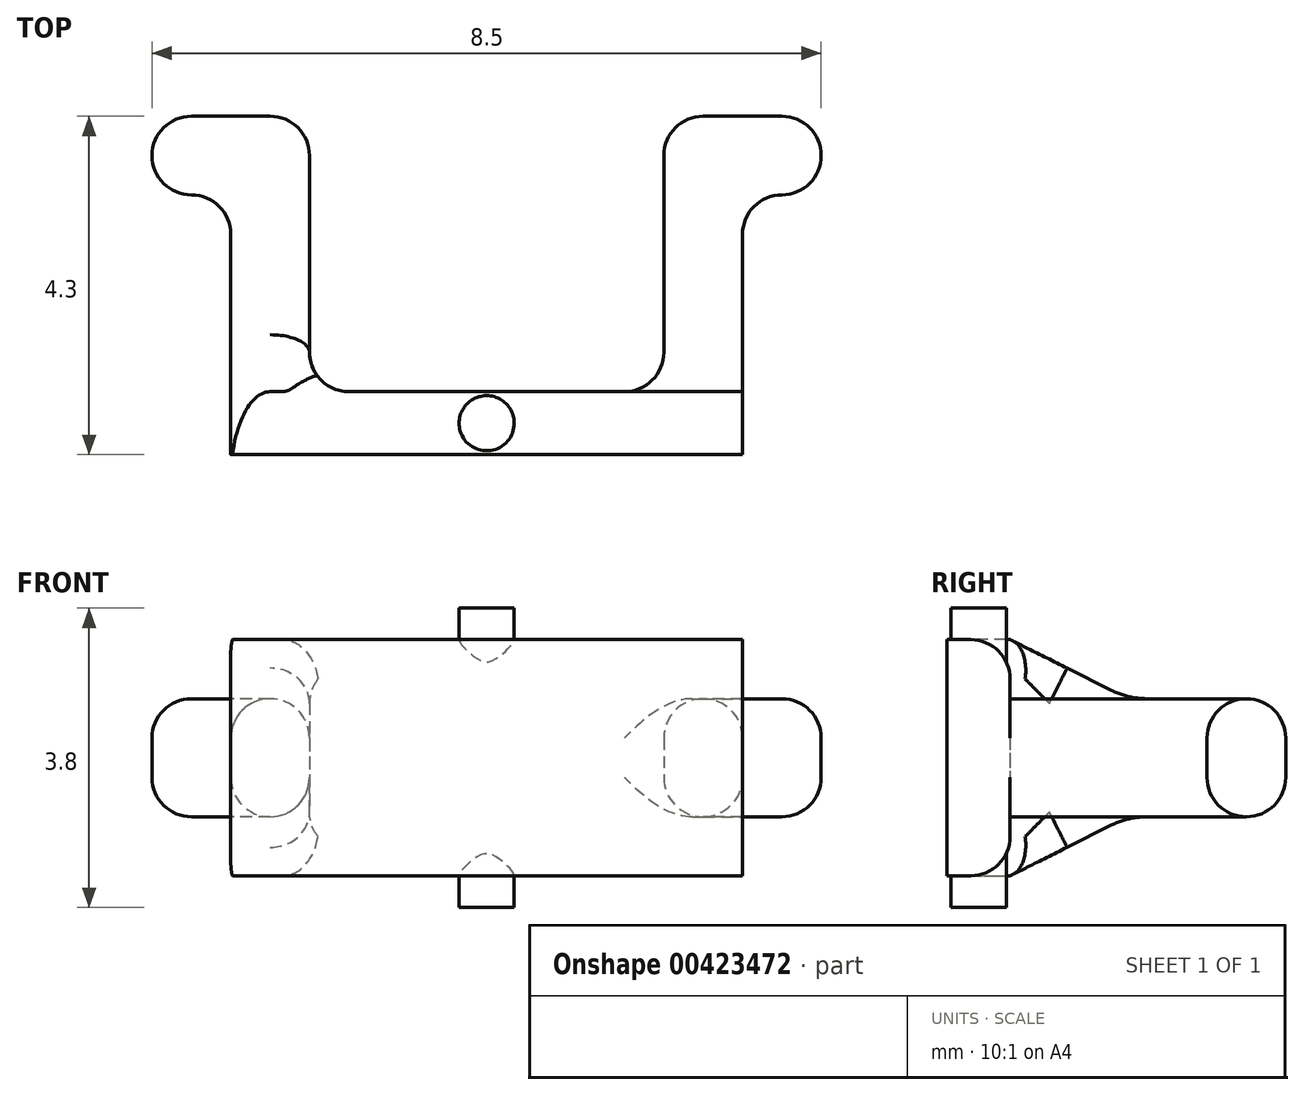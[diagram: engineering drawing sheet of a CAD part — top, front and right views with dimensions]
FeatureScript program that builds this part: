
annotation { "Feature Type Name" : "Feature", "Feature Type Description" : "" }
export const myFeature = defineFeature(function(context is Context, id is Id, definition is map)
    precondition{}
    {
        {
            var Q0;
            Q0=qCreatedBy(makeId("Top.planeOp"),FACE);
            var sketch = newSketch(context, id + "F0", { "sketchPlane" : qUnion([Q0])});
            skLineSegment(sketch, "E0", {"start": v(-3.25, 0) * mm, "end": v(3.25, 0) * mm});
            skPoint(sketch, "E1", {"position": v(0, 0) * mm});
            skLineSegment(sketch, "E2", {"start": v(0, -3) * mm, "end": v(0, 7.11) * mm, "construction": true});
            skLineSegment(sketch, "E3", {"start": v(2.25, 1.3) * mm, "end": v(2.25, 3.8) * mm});
            skLineSegment(sketch, "E4", {"start": v(-2.25, 1.3) * mm, "end": v(-2.25, 3.8) * mm});
            skLineSegment(sketch, "E5", {"start": v(-1.75, 0.8) * mm, "end": v(1.75, 0.8) * mm});
            skPoint(sketch, "E6", {"position": v(0, 0.8) * mm});
            skLineSegment(sketch, "E7", {"start": v(-2.75, 4.3) * mm, "end": v(-3.75, 4.3) * mm});
            skLineSegment(sketch, "E8", {"start": v(2.75, 4.3) * mm, "end": v(3.75, 4.3) * mm});
            skLineSegment(sketch, "E9", {"start": v(-4.25, 3.8) * mm, "end": v(-4.25, 3.8) * mm});
            skLineSegment(sketch, "E10", {"start": v(-3.75, 3.3) * mm, "end": v(-3.75, 3.3) * mm});
            skLineSegment(sketch, "E11", {"start": v(-3.25, 2.8) * mm, "end": v(-3.25, 0) * mm});
            skLineSegment(sketch, "E12", {"start": v(4.25, 3.8) * mm, "end": v(4.25, 3.8) * mm});
            skLineSegment(sketch, "E13", {"start": v(3.75, 3.3) * mm, "end": v(3.75, 3.3) * mm});
            skLineSegment(sketch, "E14", {"start": v(3.25, 2.8) * mm, "end": v(3.25, 0) * mm});
            skPoint(sketch, "E15.visualSharp", {"position": v(-2.25, 0.8) * mm});
            skArc(sketch, "E15.filletArc", {"start": v(-2.25, 1.3) * mm, "mid": v(-2.1, 0.95) * mm, "end": v(-1.75, 0.8) * mm});
            skPoint(sketch, "E16.visualSharp", {"position": v(2.25, 0.8) * mm});
            skArc(sketch, "E16.filletArc", {"start": v(1.75, 0.8) * mm, "mid": v(2.1, 0.95) * mm, "end": v(2.25, 1.3) * mm});
            skPoint(sketch, "E17.visualSharp", {"position": v(3.25, 3.3) * mm});
            skArc(sketch, "E17.filletArc", {"start": v(3.75, 3.3) * mm, "mid": v(3.4, 3.15) * mm, "end": v(3.25, 2.8) * mm});
            skPoint(sketch, "E18.visualSharp", {"position": v(-3.25, 3.3) * mm});
            skArc(sketch, "E18.filletArc", {"start": v(-3.25, 2.8) * mm, "mid": v(-3.4, 3.15) * mm, "end": v(-3.75, 3.3) * mm});
            skPoint(sketch, "E19.visualSharp", {"position": v(-2.25, 4.3) * mm});
            skArc(sketch, "E19.filletArc", {"start": v(-2.25, 3.8) * mm, "mid": v(-2.4, 4.15) * mm, "end": v(-2.75, 4.3) * mm});
            skPoint(sketch, "E20.visualSharp", {"position": v(2.25, 4.3) * mm});
            skArc(sketch, "E20.filletArc", {"start": v(2.75, 4.3) * mm, "mid": v(2.4, 4.15) * mm, "end": v(2.25, 3.8) * mm});
            skPoint(sketch, "E21.visualSharp", {"position": v(4.25, 4.3) * mm});
            skArc(sketch, "E21.filletArc", {"start": v(4.25, 3.8) * mm, "mid": v(4.1, 4.15) * mm, "end": v(3.75, 4.3) * mm});
            skPoint(sketch, "E22.visualSharp", {"position": v(4.25, 3.3) * mm});
            skArc(sketch, "E22.filletArc", {"start": v(3.75, 3.3) * mm, "mid": v(4.1, 3.45) * mm, "end": v(4.25, 3.8) * mm});
            skPoint(sketch, "E23.visualSharp", {"position": v(-4.25, 4.3) * mm});
            skArc(sketch, "E23.filletArc", {"start": v(-3.75, 4.3) * mm, "mid": v(-4.1, 4.15) * mm, "end": v(-4.25, 3.8) * mm});
            skPoint(sketch, "E24.visualSharp", {"position": v(-4.25, 3.3) * mm});
            skArc(sketch, "E24.filletArc", {"start": v(-4.25, 3.8) * mm, "mid": v(-4.1, 3.45) * mm, "end": v(-3.75, 3.3) * mm});
            skPoint(sketch, "E25.orphan", {"position": v(5, 0) * mm});
            skSolve(sketch);
        }
        {
            var Q0;
            Q0=qSketchRegion(id+"F0",true);
            extrude(context, id + "F1", {"entities" : qUnion([Q0]), "depth" : 1.5 * mm, "offsetDistance" : 25 * mm});
        }
        {
            var Q0;
            Q0=makeQuery(id+"F1.opExtrude","CAP_FACE",FACE,{"disambiguationData":[OSD([sQuery(id+"F0.wireOp",EDGE,"E0"),sQuery(id+"F0.wireOp",EDGE,"6YUp3G7D-HScl-yHn5-GseC-h8JY3a3RTnfq"),sQuery(id+"F0.wireOp",EDGE,"Xoj59s7T-2QtX-ZDX5-LiLJ-oQHR1xyVejqm"),sQuery(id+"F0.wireOp",EDGE,"Zc0sCTJD-TUej-OjTx-Aevo-d0EqPVeEhSTX"),sQuery(id+"F0.wireOp",EDGE,"E3"),sQuery(id+"F0.wireOp",EDGE,"E4"),sQuery(id+"F0.wireOp",EDGE,"fb0ed693-0343-43f7-9de8-dc647e30bef6.trimOffspring"),sQuery(id+"F0.wireOp",EDGE,"E5"),sQuery(id+"F0.wireOp",EDGE,"E7"),sQuery(id+"F0.wireOp",EDGE,"E8"),sQuery(id+"F0.wireOp",EDGE,"E15.filletArc"),sQuery(id+"F0.wireOp",EDGE,"E16.filletArc"),sQuery(id+"F0.wireOp",EDGE,"e3a1806a-2c86-475e-80ef-7f3d2f1d7afe.filletArc"),sQuery(id+"F0.wireOp",EDGE,"E17.filletArc"),sQuery(id+"F0.wireOp",EDGE,"63802826-9469-4e69-9e87-4bd683e02e6c.filletArc"),sQuery(id+"F0.wireOp",EDGE,"E18.filletArc"),sQuery(id+"F0.wireOp",EDGE,"E19.filletArc"),sQuery(id+"F0.wireOp",EDGE,"E20.filletArc"),sQuery(id+"F0.wireOp",EDGE,"E21.filletArc"),sQuery(id+"F0.wireOp",EDGE,"E22.filletArc"),sQuery(id+"F0.wireOp",EDGE,"E23.filletArc"),sQuery(id+"F0.wireOp",EDGE,"E24.filletArc")])],"isStart":false});
            var sketch = newSketch(context, id + "F2", { "sketchPlane" : qUnion([Q0])});
            skLineSegment(sketch, "E26.0", {"start": v(-3.25, 0) * mm, "end": v(-3.25, 0) * mm});
            skLineSegment(sketch, "E27.0", {"start": v(-3.25, 0) * mm, "end": v(-3.25, 0.8) * mm});
            skLineSegment(sketch, "E28", {"start": v(-3.25, 0.8) * mm, "end": v(3.25, 0.8) * mm});
            skLineSegment(sketch, "E29.0", {"start": v(-3.25, 0) * mm, "end": v(3.25, 0) * mm});
            skLineSegment(sketch, "E30.0", {"start": v(3.25, 0.8) * mm, "end": v(3.25, 0) * mm});
            skPoint(sketch, "E31.orphan", {"position": v(3.25, 2.8) * mm});
            skSolve(sketch);
        }
        {
            var Q0;
            Q0=qSketchRegion(id+"F2",true);
            extrude(context, id + "F3", {"entities" : qUnion([Q0]), "operationType" : NewBodyOperationType.ADD, "depth" : 0.75 * mm, "offsetDistance" : 25 * mm});
        }
        {
            var Q0;
            Q0=makeQuery(id+"F1.opExtrude","CAP_FACE",FACE,{"disambiguationData":[OSD([sQuery(id+"F0.wireOp",EDGE,"E0"),sQuery(id+"F0.wireOp",EDGE,"E3"),sQuery(id+"F0.wireOp",EDGE,"E4"),sQuery(id+"F0.wireOp",EDGE,"E5"),sQuery(id+"F0.wireOp",EDGE,"E7"),sQuery(id+"F0.wireOp",EDGE,"E8"),sQuery(id+"F0.wireOp",EDGE,"E11"),sQuery(id+"F0.wireOp",EDGE,"E14"),sQuery(id+"F0.wireOp",EDGE,"E15.filletArc"),sQuery(id+"F0.wireOp",EDGE,"E16.filletArc"),sQuery(id+"F0.wireOp",EDGE,"E17.filletArc"),sQuery(id+"F0.wireOp",EDGE,"E18.filletArc"),sQuery(id+"F0.wireOp",EDGE,"E19.filletArc"),sQuery(id+"F0.wireOp",EDGE,"E20.filletArc"),sQuery(id+"F0.wireOp",EDGE,"E21.filletArc"),sQuery(id+"F0.wireOp",EDGE,"E22.filletArc"),sQuery(id+"F0.wireOp",EDGE,"E23.filletArc"),sQuery(id+"F0.wireOp",EDGE,"E24.filletArc")])],"isStart":true});
            var sketch = newSketch(context, id + "F4", { "sketchPlane" : qUnion([Q0])});
            skLineSegment(sketch, "E32.0", {"start": v(-3.25, 0) * mm, "end": v(-3.25, -0.8) * mm});
            skLineSegment(sketch, "E33.0", {"start": v(-3.25, -0.8) * mm, "end": v(3.25, -0.8) * mm});
            skLineSegment(sketch, "E34.0", {"start": v(-3.25, 0) * mm, "end": v(3.25, 0) * mm});
            skLineSegment(sketch, "E35.0", {"start": v(3.25, -0.8) * mm, "end": v(3.25, 0) * mm});
            skSolve(sketch);
        }
        {
            var Q0;
            Q0=qSketchRegion(id+"F4",true);
            extrude(context, id + "F5", {"entities" : qUnion([Q0]), "operationType" : NewBodyOperationType.ADD, "depth" : 0.75 * mm, "offsetDistance" : 25 * mm});
        }
        {
            var Q0;
            {var subQ4=sQuery(id+"F0.wireOp",EDGE,"E15.filletArc");var subQ5=sQuery(id+"F2.wireOp",EDGE,"E28");Q0=makeQuery(id+"F3.boolean.opBoolean","SPLIT",EDGE,{"disambiguationData":[TD([makeQuery(id+"F1.opExtrude","SWEPT_FACE",FACE,{"disambiguationData":[OSD([subQ4])]})])],"derivedFrom":makeQuery(id+"F3.opExtrude","CAP_EDGE",EDGE,{"disambiguationData":[OSD([subQ5])],"isStart":true})});}
            var Q1;
            {var subQ3=sQuery(id+"F0.wireOp",EDGE,"E16.filletArc");var subQ5=sQuery(id+"F2.wireOp",EDGE,"E28");Q1=makeQuery(id+"F3.boolean.opBoolean","SPLIT",EDGE,{"disambiguationData":[TD([makeQuery(id+"F1.opExtrude","SWEPT_FACE",FACE,{"disambiguationData":[OSD([subQ3])]})])],"derivedFrom":makeQuery(id+"F3.opExtrude","CAP_EDGE",EDGE,{"disambiguationData":[OSD([subQ5])],"isStart":true})});}
            chamfer(context, id + "F6", {"entities" : qUnion([Q0, Q1]), "chamferType" : ChamferType.TWO_OFFSETS, "width1" : 1.5 * mm, "oppositeDirection" : false, "width2" : 0.75 * mm, "tangentPropagation" : true});
        }
        {
            var Q0;
            {var subQ0=sQuery(id+"F0.wireOp",EDGE,"E14");var subQ1=sQuery(id+"F4.wireOp",EDGE,"E33.0");Q0=makeQuery(id+"F5.boolean.opBoolean","SPLIT",EDGE,{"disambiguationData":[TD([makeQuery(id+"F1.opExtrude","SWEPT_FACE",FACE,{"disambiguationData":[OSD([subQ0])]})])],"derivedFrom":makeQuery(id+"F5.opExtrude","CAP_EDGE",EDGE,{"disambiguationData":[OSD([subQ1])],"isStart":true})});}
            var Q1;
            {var subQ0=sQuery(id+"F0.wireOp",EDGE,"E11");var subQ3=sQuery(id+"F4.wireOp",EDGE,"E33.0");Q1=makeQuery(id+"F5.boolean.opBoolean","SPLIT",EDGE,{"disambiguationData":[TD([makeQuery(id+"F1.opExtrude","SWEPT_FACE",FACE,{"disambiguationData":[OSD([subQ0])]})])],"derivedFrom":makeQuery(id+"F5.opExtrude","CAP_EDGE",EDGE,{"disambiguationData":[OSD([subQ3])],"isStart":true})});}
            chamfer(context, id + "F7", {"entities" : qUnion([Q0, Q1]), "chamferType" : ChamferType.TWO_OFFSETS, "width1" : 1.5 * mm, "oppositeDirection" : true, "width2" : 0.75 * mm, "tangentPropagation" : true});
        }
        {
            var Q0;
            {var subQ0=sQuery(id+"F0.wireOp",EDGE,"E20.filletArc");var subQ1=sQuery(id+"F0.wireOp",EDGE,"e3a1806a-2c86-475e-80ef-7f3d2f1d7afe.filletArc");var subQ3=sQuery(id+"F0.wireOp",EDGE,"E14");var subQ4=sQuery(id+"F0.wireOp",EDGE,"E8");var subQ5=sQuery(id+"F0.wireOp",EDGE,"E16.filletArc");var subQ6=makeQuery(id+"F1.opExtrude","SWEPT_FACE",FACE,{"disambiguationData":[OSD([subQ5])]});var subQ7=sQuery(id+"F0.wireOp",EDGE,"Xoj59s7T-2QtX-ZDX5-LiLJ-oQHR1xyVejqm");var subQ9=sQuery(id+"F0.wireOp",EDGE,"E5");var subQ11=sQuery(id+"F2.wireOp",EDGE,"E28");var subQ13=sQuery(id+"F0.wireOp",EDGE,"E17.filletArc");var subQ14=sQuery(id+"F0.wireOp",EDGE,"E3");var subQ15=sQuery(id+"F0.wireOp",EDGE,"fb0ed693-0343-43f7-9de8-dc647e30bef6.trimOffspring");var subQ17=sQuery(id+"F0.wireOp",EDGE,"E22.filletArc");var subQ18=sQuery(id+"F0.wireOp",EDGE,"E21.filletArc");var subQ19=makeQuery(id+"F1.opExtrude","CAP_FACE",FACE,{"disambiguationData":[OSD([sQuery(id+"F0.wireOp",EDGE,"E0"),sQuery(id+"F0.wireOp",EDGE,"6YUp3G7D-HScl-yHn5-GseC-h8JY3a3RTnfq"),subQ7,sQuery(id+"F0.wireOp",EDGE,"Zc0sCTJD-TUej-OjTx-Aevo-d0EqPVeEhSTX"),subQ14,sQuery(id+"F0.wireOp",EDGE,"E4"),subQ15,subQ9,sQuery(id+"F0.wireOp",EDGE,"E7"),subQ4,sQuery(id+"F0.wireOp",EDGE,"E11"),subQ3,sQuery(id+"F0.wireOp",EDGE,"E15.filletArc"),subQ5,subQ1,subQ13,sQuery(id+"F0.wireOp",EDGE,"63802826-9469-4e69-9e87-4bd683e02e6c.filletArc"),sQuery(id+"F0.wireOp",EDGE,"E18.filletArc"),sQuery(id+"F0.wireOp",EDGE,"E19.filletArc"),subQ0,subQ18,subQ17,sQuery(id+"F0.wireOp",EDGE,"E23.filletArc"),sQuery(id+"F0.wireOp",EDGE,"E24.filletArc")])],"isStart":false});Q0=makeQuery(id+"F6.opChamfer","BLEND_EDGE",EDGE,{"blendedFrom":[makeQuery(id+"F3.boolean.opBoolean","SPLIT",EDGE,{"disambiguationData":[TD([subQ6])],"derivedFrom":makeQuery(id+"F3.opExtrude","CAP_EDGE",EDGE,{"disambiguationData":[OSD([subQ11])],"isStart":true})}),makeQuery(id+"F3.boolean.opBoolean","SPLIT",FACE,{"disambiguationData":[TD([makeQuery(id+"F1.opExtrude","SWEPT_FACE",FACE,{"disambiguationData":[OSD([subQ14])]})])],"derivedFrom":subQ19})],"blendedInto":[makeQuery(id+"F3.boolean.opBoolean","SPLIT",FACE,{"disambiguationData":[TD([makeQuery(id+"F1.opExtrude","SWEPT_FACE",FACE,{"disambiguationData":[OSD([subQ14])]})])],"derivedFrom":subQ19})]});}
            var Q1;
            {var subQ0=sQuery(id+"F0.wireOp",EDGE,"E15.filletArc");var subQ1=makeQuery(id+"F1.opExtrude","SWEPT_FACE",FACE,{"disambiguationData":[OSD([subQ0])]});var subQ2=sQuery(id+"F0.wireOp",EDGE,"E11");var subQ3=sQuery(id+"F0.wireOp",EDGE,"E7");var subQ4=sQuery(id+"F0.wireOp",EDGE,"Xoj59s7T-2QtX-ZDX5-LiLJ-oQHR1xyVejqm");var subQ6=sQuery(id+"F0.wireOp",EDGE,"E19.filletArc");var subQ7=sQuery(id+"F0.wireOp",EDGE,"E5");var subQ9=sQuery(id+"F2.wireOp",EDGE,"E28");var subQ11=sQuery(id+"F0.wireOp",EDGE,"63802826-9469-4e69-9e87-4bd683e02e6c.filletArc");var subQ13=sQuery(id+"F0.wireOp",EDGE,"E4");var subQ14=sQuery(id+"F0.wireOp",EDGE,"E18.filletArc");var subQ15=sQuery(id+"F0.wireOp",EDGE,"fb0ed693-0343-43f7-9de8-dc647e30bef6.trimOffspring");var subQ17=sQuery(id+"F0.wireOp",EDGE,"E24.filletArc");var subQ18=sQuery(id+"F0.wireOp",EDGE,"E23.filletArc");var subQ19=makeQuery(id+"F1.opExtrude","CAP_FACE",FACE,{"disambiguationData":[OSD([sQuery(id+"F0.wireOp",EDGE,"E0"),sQuery(id+"F0.wireOp",EDGE,"6YUp3G7D-HScl-yHn5-GseC-h8JY3a3RTnfq"),subQ4,sQuery(id+"F0.wireOp",EDGE,"Zc0sCTJD-TUej-OjTx-Aevo-d0EqPVeEhSTX"),sQuery(id+"F0.wireOp",EDGE,"E3"),subQ13,subQ15,subQ7,subQ3,sQuery(id+"F0.wireOp",EDGE,"E8"),subQ2,sQuery(id+"F0.wireOp",EDGE,"E14"),subQ0,sQuery(id+"F0.wireOp",EDGE,"E16.filletArc"),sQuery(id+"F0.wireOp",EDGE,"e3a1806a-2c86-475e-80ef-7f3d2f1d7afe.filletArc"),sQuery(id+"F0.wireOp",EDGE,"E17.filletArc"),subQ11,subQ14,subQ6,sQuery(id+"F0.wireOp",EDGE,"E20.filletArc"),sQuery(id+"F0.wireOp",EDGE,"E21.filletArc"),sQuery(id+"F0.wireOp",EDGE,"E22.filletArc"),subQ18,subQ17])],"isStart":false});Q1=makeQuery(id+"F6.opChamfer","BLEND_EDGE",EDGE,{"blendedFrom":[makeQuery(id+"F3.boolean.opBoolean","SPLIT",EDGE,{"disambiguationData":[TD([subQ1])],"derivedFrom":makeQuery(id+"F3.opExtrude","CAP_EDGE",EDGE,{"disambiguationData":[OSD([subQ9])],"isStart":true})}),makeQuery(id+"F3.boolean.opBoolean","SPLIT",FACE,{"disambiguationData":[TD([makeQuery(id+"F1.opExtrude","SWEPT_FACE",FACE,{"disambiguationData":[OSD([subQ13])]})])],"derivedFrom":subQ19})],"blendedInto":[makeQuery(id+"F3.boolean.opBoolean","SPLIT",FACE,{"disambiguationData":[TD([makeQuery(id+"F1.opExtrude","SWEPT_FACE",FACE,{"disambiguationData":[OSD([subQ13])]})])],"derivedFrom":subQ19})]});}
            var Q2;
            {var subQ1=sQuery(id+"F0.wireOp",EDGE,"E14");var subQ2=makeQuery(id+"F1.opExtrude","SWEPT_FACE",FACE,{"disambiguationData":[OSD([subQ1])]});var subQ4=sQuery(id+"F0.wireOp",EDGE,"E8");var subQ5=sQuery(id+"F0.wireOp",EDGE,"E20.filletArc");var subQ6=sQuery(id+"F0.wireOp",EDGE,"E17.filletArc");var subQ7=sQuery(id+"F0.wireOp",EDGE,"E16.filletArc");var subQ9=sQuery(id+"F0.wireOp",EDGE,"E3");var subQ10=sQuery(id+"F0.wireOp",EDGE,"E22.filletArc");var subQ11=sQuery(id+"F0.wireOp",EDGE,"E21.filletArc");var subQ12=sQuery(id+"F0.wireOp",EDGE,"E5");var subQ14=sQuery(id+"F4.wireOp",EDGE,"E33.0");var subQ17=makeQuery(id+"F1.opExtrude","CAP_FACE",FACE,{"disambiguationData":[OSD([sQuery(id+"F0.wireOp",EDGE,"E0"),subQ9,sQuery(id+"F0.wireOp",EDGE,"E4"),subQ12,sQuery(id+"F0.wireOp",EDGE,"E7"),subQ4,sQuery(id+"F0.wireOp",EDGE,"E11"),subQ1,sQuery(id+"F0.wireOp",EDGE,"E15.filletArc"),subQ7,subQ6,sQuery(id+"F0.wireOp",EDGE,"E18.filletArc"),sQuery(id+"F0.wireOp",EDGE,"E19.filletArc"),subQ5,subQ11,subQ10,sQuery(id+"F0.wireOp",EDGE,"E23.filletArc"),sQuery(id+"F0.wireOp",EDGE,"E24.filletArc")])],"isStart":true});Q2=makeQuery(id+"F7.opChamfer","BLEND_EDGE",EDGE,{"blendedFrom":[makeQuery(id+"F5.boolean.opBoolean","SPLIT",EDGE,{"disambiguationData":[TD([subQ2])],"derivedFrom":makeQuery(id+"F5.opExtrude","CAP_EDGE",EDGE,{"disambiguationData":[OSD([subQ14])],"isStart":true})}),makeQuery(id+"F5.boolean.opBoolean","SPLIT",FACE,{"disambiguationData":[TD([makeQuery(id+"F1.opExtrude","SWEPT_FACE",FACE,{"disambiguationData":[OSD([subQ9])]})])],"derivedFrom":subQ17})],"blendedInto":[makeQuery(id+"F5.boolean.opBoolean","SPLIT",FACE,{"disambiguationData":[TD([makeQuery(id+"F1.opExtrude","SWEPT_FACE",FACE,{"disambiguationData":[OSD([subQ9])]})])],"derivedFrom":subQ17})]});}
            var Q3;
            {var subQ1=sQuery(id+"F0.wireOp",EDGE,"E4");var subQ2=sQuery(id+"F0.wireOp",EDGE,"E19.filletArc");var subQ3=sQuery(id+"F0.wireOp",EDGE,"E18.filletArc");var subQ4=sQuery(id+"F0.wireOp",EDGE,"E15.filletArc");var subQ7=sQuery(id+"F0.wireOp",EDGE,"E5");var subQ9=sQuery(id+"F0.wireOp",EDGE,"E24.filletArc");var subQ10=sQuery(id+"F0.wireOp",EDGE,"E23.filletArc");var subQ12=sQuery(id+"F0.wireOp",EDGE,"E7");var subQ13=sQuery(id+"F0.wireOp",EDGE,"E11");var subQ14=makeQuery(id+"F1.opExtrude","SWEPT_FACE",FACE,{"disambiguationData":[OSD([subQ13])]});var subQ15=sQuery(id+"F4.wireOp",EDGE,"E33.0");var subQ17=makeQuery(id+"F1.opExtrude","CAP_FACE",FACE,{"disambiguationData":[OSD([sQuery(id+"F0.wireOp",EDGE,"E0"),sQuery(id+"F0.wireOp",EDGE,"E3"),subQ1,subQ7,subQ12,sQuery(id+"F0.wireOp",EDGE,"E8"),subQ13,sQuery(id+"F0.wireOp",EDGE,"E14"),subQ4,sQuery(id+"F0.wireOp",EDGE,"E16.filletArc"),sQuery(id+"F0.wireOp",EDGE,"E17.filletArc"),subQ3,subQ2,sQuery(id+"F0.wireOp",EDGE,"E20.filletArc"),sQuery(id+"F0.wireOp",EDGE,"E21.filletArc"),sQuery(id+"F0.wireOp",EDGE,"E22.filletArc"),subQ10,subQ9])],"isStart":true});Q3=makeQuery(id+"F7.opChamfer","BLEND_EDGE",EDGE,{"blendedFrom":[makeQuery(id+"F5.boolean.opBoolean","SPLIT",EDGE,{"disambiguationData":[TD([subQ14])],"derivedFrom":makeQuery(id+"F5.opExtrude","CAP_EDGE",EDGE,{"disambiguationData":[OSD([subQ15])],"isStart":true})}),makeQuery(id+"F5.boolean.opBoolean","SPLIT",FACE,{"disambiguationData":[TD([makeQuery(id+"F1.opExtrude","SWEPT_FACE",FACE,{"disambiguationData":[OSD([subQ1])]})])],"derivedFrom":subQ17})],"blendedInto":[makeQuery(id+"F5.boolean.opBoolean","SPLIT",FACE,{"disambiguationData":[TD([makeQuery(id+"F1.opExtrude","SWEPT_FACE",FACE,{"disambiguationData":[OSD([subQ1])]})])],"derivedFrom":subQ17})]});}
            fillet(context, id + "F8", {"entities" : qUnion([Q0, Q1, Q2, Q3]), "radius" : 1 * mm, "tangentPropagation" : true, "defaultsChanged" : false, "vertexSettings" : [], "allowEdgeOverflow" : false});
        }
        {
            var Q0;
            Q0=makeQuery(id+"F3.opExtrude","CAP_EDGE",EDGE,{"disambiguationData":[OSD([sQuery(id+"F2.wireOp",EDGE,"E28")])],"isStart":false});
            var Q1;
            Q1=makeQuery(id+"F1.opExtrude","CAP_EDGE",EDGE,{"disambiguationData":[OSD([sQuery(id+"F0.wireOp",EDGE,"E8")])],"isStart":false});
            var Q2;
            Q2=makeQuery(id+"F1.opExtrude","CAP_EDGE",EDGE,{"disambiguationData":[OSD([sQuery(id+"F0.wireOp",EDGE,"E7")])],"isStart":false});
            var Q3;
            Q3=makeQuery(id+"F5.opExtrude","CAP_EDGE",EDGE,{"disambiguationData":[OSD([sQuery(id+"F4.wireOp",EDGE,"E33.0")])],"isStart":false});
            var Q4;
            Q4=makeQuery(id+"F1.opExtrude","CAP_EDGE",EDGE,{"disambiguationData":[OSD([sQuery(id+"F0.wireOp",EDGE,"E8")])],"isStart":true});
            var Q5;
            Q5=makeQuery(id+"F1.opExtrude","CAP_EDGE",EDGE,{"disambiguationData":[OSD([sQuery(id+"F0.wireOp",EDGE,"E7")])],"isStart":true});
            fillet(context, id + "F9", {"entities" : qUnion([Q0, Q1, Q2, Q3, Q4, Q5]), "radius" : 0.5 * mm, "tangentPropagation" : true, "defaultsChanged" : false, "vertexSettings" : [], "allowEdgeOverflow" : false});
        }
        {
            var Q0;
            Q0=makeQuery(id+"F3.opExtrude","CAP_FACE",FACE,{"disambiguationData":[OSD([sQuery(id+"F2.wireOp",EDGE,"E27.0"),sQuery(id+"F2.wireOp",EDGE,"E28"),sQuery(id+"F2.wireOp",EDGE,"E29.0"),sQuery(id+"F2.wireOp",EDGE,"E30.0")])],"isStart":false});
            var sketch = newSketch(context, id + "F10", { "sketchPlane" : qUnion([Q0])});
            skLineSegment(sketch, "E36.0", {"start": v(-3.23, 0) * mm, "end": v(3.23, 0) * mm, "construction": true});
            skLineSegment(sketch, "E37.0", {"start": v(-1.75, 0.8) * mm, "end": v(1.75, 0.8) * mm, "construction": true});
            skPoint(sketch, "E38", {"position": v(0, 0) * mm});
            skPoint(sketch, "E39", {"position": v(0, 0.8) * mm});
            skLineSegment(sketch, "E40", {"start": v(0, 0.8) * mm, "end": v(0, 0) * mm, "construction": true});
            skPoint(sketch, "E41", {"position": v(0, 0.4) * mm});
            skCircle(sketch, "E42", {"center": v(0, 0.4) * mm, "radius": 0.35 * mm});
            skSolve(sketch);
        }
        {
            var Q0;
            Q0=qSketchRegion(id+"F10",true);
            extrude(context, id + "F11", {"entities" : qUnion([Q0]), "operationType" : NewBodyOperationType.ADD, "depth" : 0.4 * mm, "offsetDistance" : 25 * mm, "hasSecondDirection" : true, "secondDirectionOppositeDirection" : true, "secondDirectionDepth" : 3.4 * mm});
        }
    });
